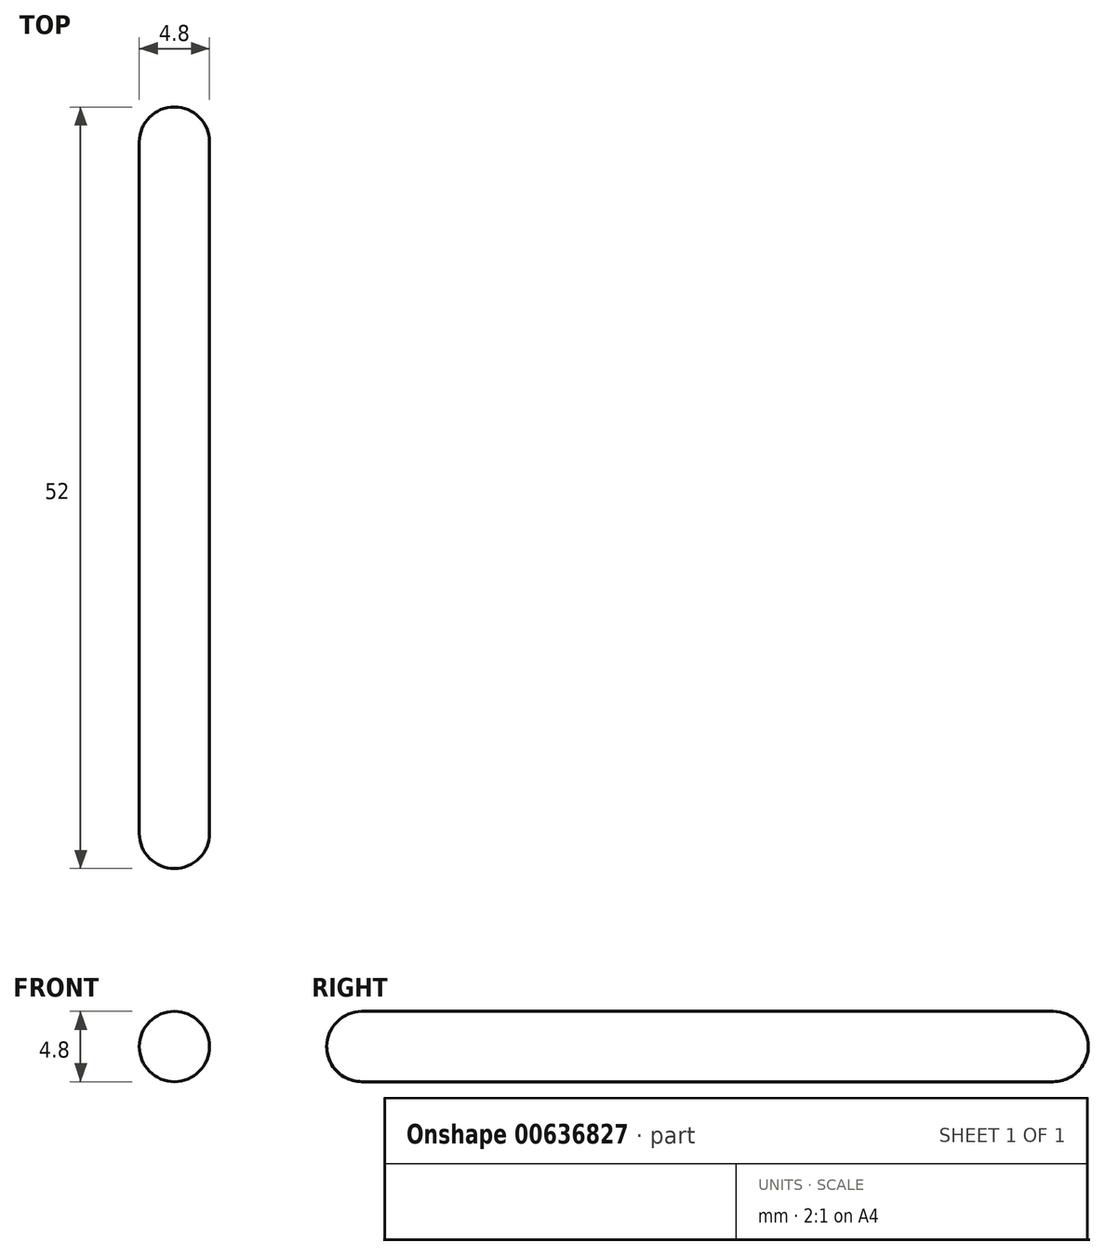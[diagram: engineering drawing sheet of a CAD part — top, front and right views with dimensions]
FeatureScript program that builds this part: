
annotation { "Feature Type Name" : "Feature", "Feature Type Description" : "" }
export const myFeature = defineFeature(function(context is Context, id is Id, definition is map)
    precondition{}
    {
        {
            var Q0;
            Q0=qCreatedBy(makeId("Front.planeOp"),FACE);
            var sketch = newSketch(context, id + "F0", { "sketchPlane" : qUnion([Q0])});
            skCircle(sketch, "E0", {"center": v(0, 0) * mm, "radius": 2.4 * mm});
            skSolve(sketch);
        }
        {
            var Q0;
            Q0=makeQuery(id+"F0.imprint","IMPRINT",FACE,{"disambiguationData":[TD([[makeQuery(id+"F0.imprint","IMPRINT",EDGE,{"derivedFrom":sQuery(id+"F0.wireOp",EDGE,"E0")}),1.0]])]});
            extrude(context, id + "F1", {"entities" : qUnion([Q0]), "depth" : 52 * mm, "offsetDistance" : 25 * mm, "symmetric" : true});
        }
        {
            var Q0;
            Q0=makeQuery(id+"F1.opExtrude","CAP_EDGE",EDGE,{"disambiguationData":[OSD([sQuery(id+"F0.wireOp",EDGE,"E0")])],"isStart":false});
            var Q1;
            Q1=makeQuery(id+"F1.opExtrude","CAP_EDGE",EDGE,{"disambiguationData":[OSD([sQuery(id+"F0.wireOp",EDGE,"E0")])],"isStart":true});
            fillet(context, id + "F2", {"entities" : qUnion([Q0, Q1]), "radius" : 2.4 * mm, "tangentPropagation" : true, "allowEdgeOverflow" : false});
        }
    });
